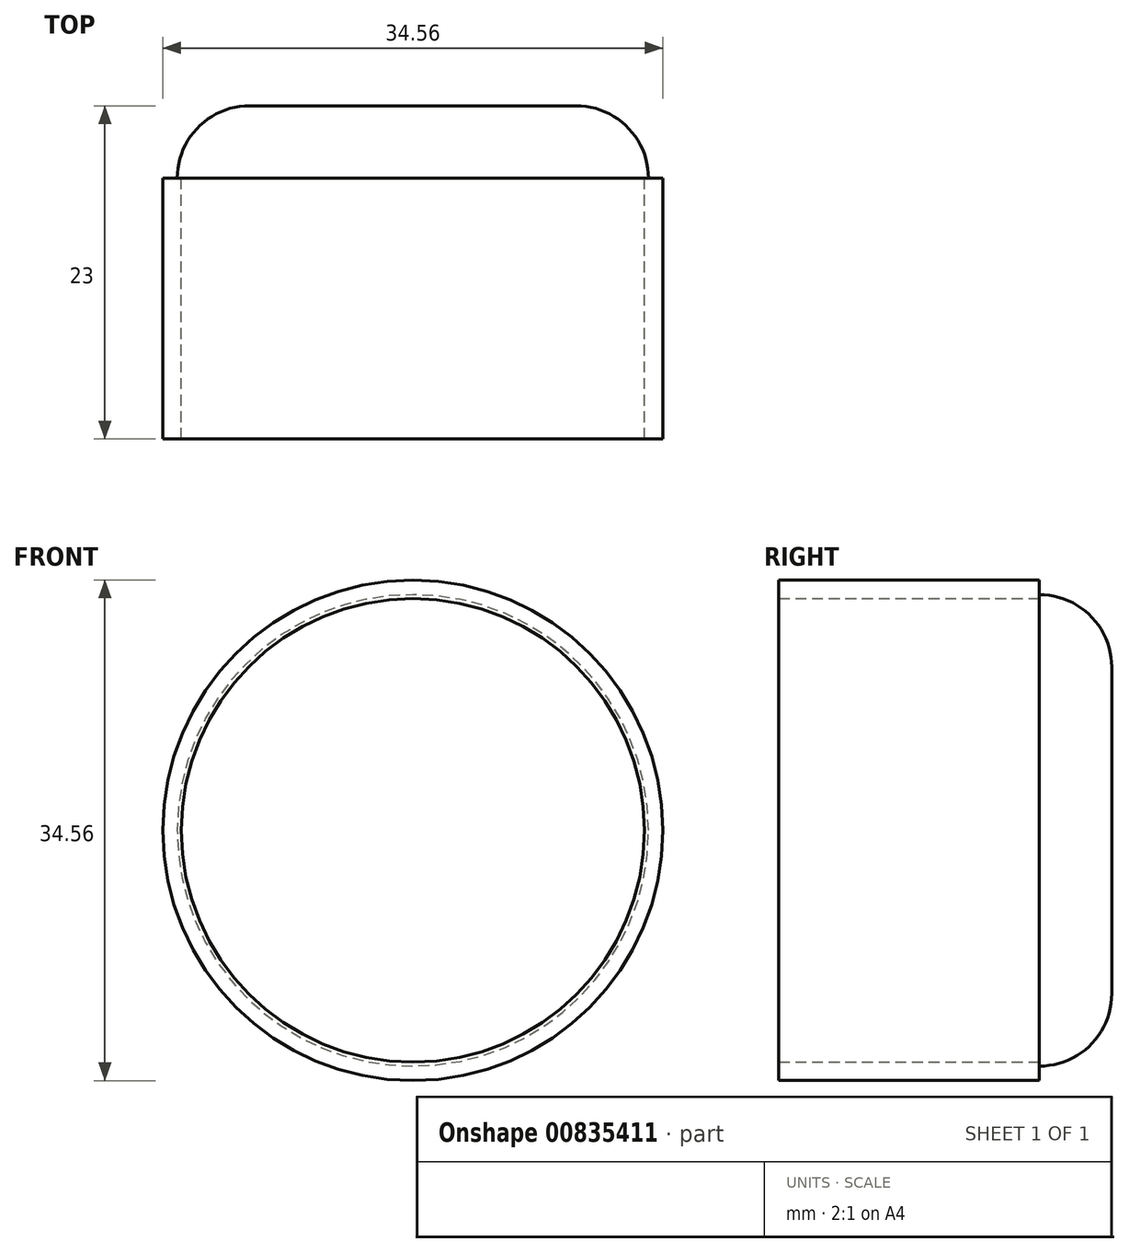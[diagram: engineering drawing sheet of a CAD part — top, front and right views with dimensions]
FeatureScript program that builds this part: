
annotation { "Feature Type Name" : "Feature", "Feature Type Description" : "" }
export const myFeature = defineFeature(function(context is Context, id is Id, definition is map)
    precondition{}
    {
        {
            var Q0;
            Q0=qCreatedBy(makeId("Front.planeOp"),FACE);
            var sketch = newSketch(context, id + "F0", { "sketchPlane" : qUnion([Q0])});
            skCircle(sketch, "E0", {"center": v(0, 0) * mm, "radius": 17.27 * mm});
            skSolve(sketch);
        }
        {
            var Q0;
            Q0 = qSketchRegion(id + "F0", true);
            extrude(context, id + "F1", {"entities" : qUnion([Q0]), "depth" : 18 * mm, "offsetDistance" : 25 * mm});
        }
        {
            var Q0;
            Q0=qCreatedBy(makeId("Front.planeOp"),FACE);
            var sketch = newSketch(context, id + "F2", { "sketchPlane" : qUnion([Q0])});
            skCircle(sketch, "E1", {"center": v(0, 0) * mm, "radius": 16 * mm});
            skSolve(sketch);
        }
        {
            var Q0;
            Q0=sQuery(id+"F2.wireOp",VERTEX,"E1.center");
            var Q1;
            Q1=makeQuery(id+"F1.opExtrude","SWEPT_BODY",BODY,{"disambiguationData":[OSD([sQuery(id+"F0.wireOp",EDGE,"E0")])]});
            hole(context, id + "F3", {"style" : HoleStyle.SIMPLE, "endStyle" : HoleEndStyle.THROUGH, "oppositeDirection" : true, "holeDiameter" : 32 * mm, "majorDiameter" : 5 * mm, "isTappedThrough" : true, "tappedDepth" : 12 * mm, "tapClearance" : 3, "locations" : qUnion([Q0]), "scope" : qUnion([Q1])});
        }
        {
            var Q0;
            Q0=qCreatedBy(makeId("Front.planeOp"),FACE);
            var sketch = newSketch(context, id + "F4", { "sketchPlane" : qUnion([Q0])});
            skCircle(sketch, "E2", {"center": v(0, 0) * mm, "radius": 16.27 * mm});
            skSolve(sketch);
        }
        {
            var Q0;
            Q0 = qSketchRegion(id + "F4", true);
            extrude(context, id + "F5", {"entities" : qUnion([Q0]), "operationType" : NewBodyOperationType.ADD, "depth" : -5 * mm, "offsetDistance" : 25 * mm});
        }
        {
            var Q0;
            Q0=makeQuery(id+"F5.opExtrude","CAP_EDGE",EDGE,{"disambiguationData":[OSD([sQuery(id+"F4.wireOp",EDGE,"E2")])],"isStart":false});
            fillet(context, id + "F6", {"entities" : qUnion([Q0]), "radius" : 5 * mm, "tangentPropagation" : true, "allowEdgeOverflow" : false});
        }
    });
